# Revit family: Trapezblechhänger LL A
name_source: partatom
category: Allgemeines Modell
revit_build: Autodesk Revit 2017 (Build: 20190507_1515(x64)
units: mm (PartAtom-declared; Revit-internal decimal feet)

## family parameters
Arbeitsebenenbasiert = Ja
Beim Laden mit Abzugskörper schneiden = Nein
Bemaßung runder Anschluss = Durchmesser verwenden
Gemeinsam genutzt = Ja
Immer vertikal = Nein
Kann Basisbauteil für Bewehrung sein = Nein
Raumberechnungspunkt = Nein
Teiletyp = Normal

## types (3) — shared parameters
Befestigungsloch = 9.5 mm
Breite Aufnahme (innen) = 22,5 mm
Breite Material = 25 mm
Fabrikat = MEFA
Firma = MEFA Befestigungs- und Montagesysteme GmbH
Material = Stahl
Materialname = S235/DD11
Mengeneinheit = St
Oberflaeche = galvanisch verzinkt
Stärke Material = 3 mm  [stored 0.00984252 ft]
Vorgabe-Ansicht = 1219 mm
vpe = 100 St

## per-type parameters (varying)
| type | Anschlussgewinde | Artikelnummer | Ausführung | EAN | Gewicht | Gewicht pro Bauteil | Höhe | Kurztext1 | Kurztext2 | Schalldämmeinlage | max. zul. Last |
| MEFA Trapezblechhänger MU-S M 8 | M8 | 0783900 | eingeschweißte Mutter | 4250928418845 | 0.11 kg | 0.11 kg | 92.5 mm | Trapezblechhänger MU-S | eingeschweißte Mutter M8 |  | 2.00 kN |
| MEFA Trapezblechhänger MU-S M10 | M10 | 0783935 | eingeschweißte Mutter | 4250928418852 | 0.12 kg | 0.12 kg | 92.5 mm | Trapezblechhänger MU-S | eingeschweißte Mutter M10 |  | 2.00 kN |
| Trapezblechhänger LL A | M8, M10 | 0783840 | mit Schalldämmelement | 4250928418838 | 0.12 kg | 0.12 kg | 925 mm | Trapezblechhänger LL A | mit Schalldämmelement M8, M10 | Gummi | 0.80 kN |

note: [stored X ft] marks values corroborated as IEEE doubles in the binary element streams (Revit-internal decimal feet)
